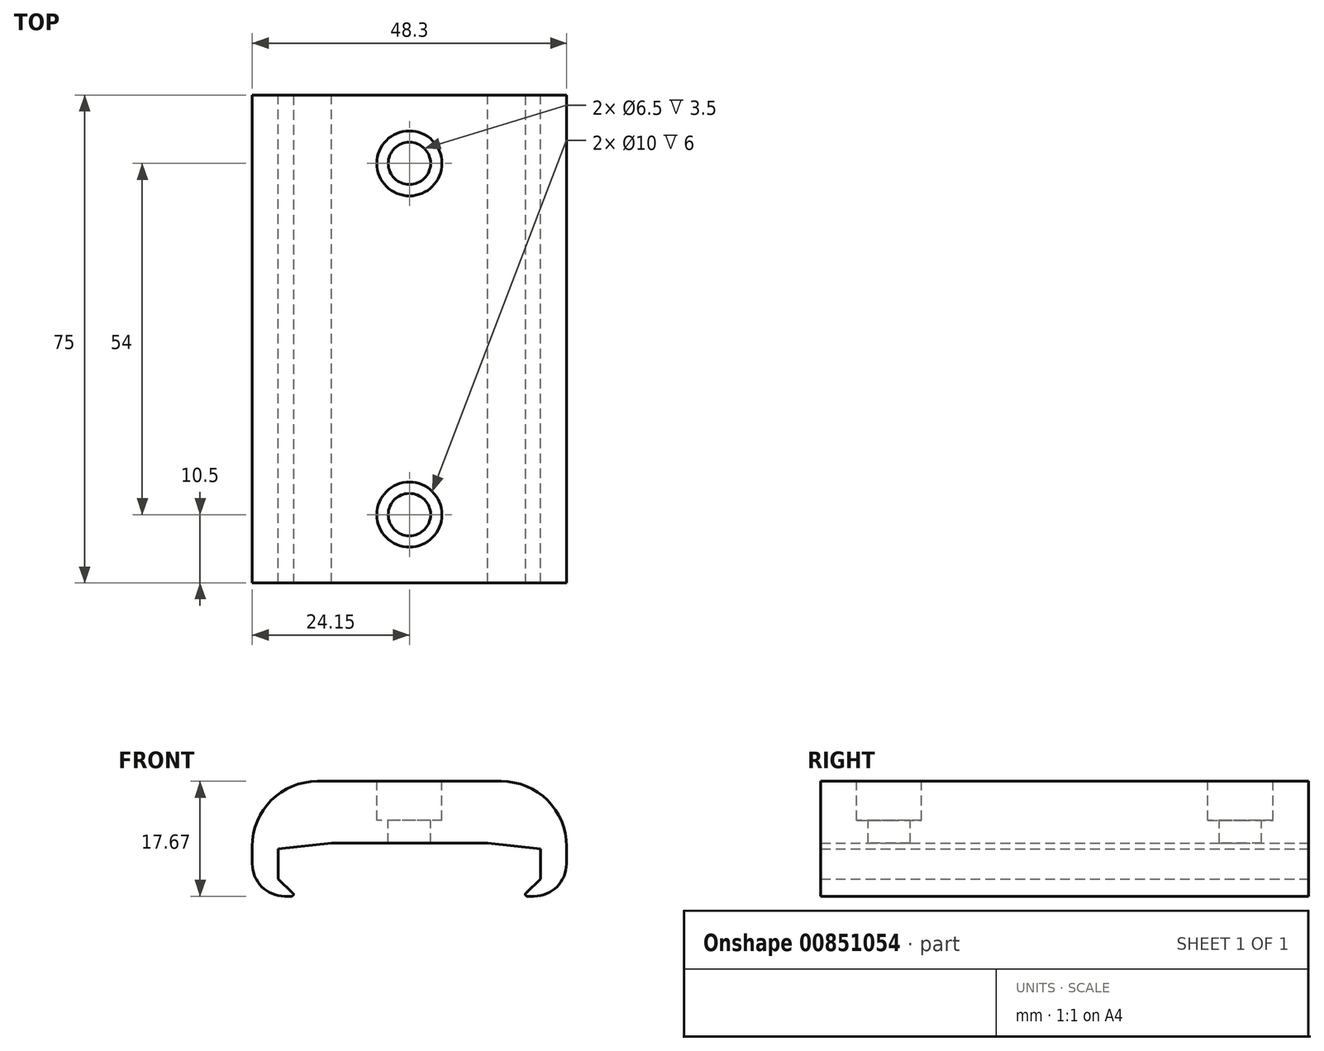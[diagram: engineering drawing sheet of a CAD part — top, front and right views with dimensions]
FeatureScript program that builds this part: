
annotation { "Feature Type Name" : "Feature", "Feature Type Description" : "" }
export const myFeature = defineFeature(function(context is Context, id is Id, definition is map)
    precondition{}
    {
        {
            var Q0;
            Q0=qCreatedBy(makeId("Front.planeOp"),FACE);
            var sketch = newSketch(context, id + "F0", { "sketchPlane" : qUnion([Q0])});
            skLineSegment(sketch, "E0.bottom", {"start": v(-12, 5.5) * mm, "end": v(12, 5.5) * mm});
            skLineSegment(sketch, "E0.left", {"start": v(-20.15, 4.6) * mm, "end": v(-20.15, 0) * mm});
            skLineSegment(sketch, "E0.right", {"start": v(20.15, 4.6) * mm, "end": v(20.15, 0) * mm});
            skLineSegment(sketch, "E1.top", {"start": v(-24.15, 15) * mm, "end": v(24.15, 15) * mm});
            skLineSegment(sketch, "E1.left", {"start": v(-24.15, 0) * mm, "end": v(-24.15, 15) * mm});
            skLineSegment(sketch, "E1.right", {"start": v(24.15, 0) * mm, "end": v(24.15, 15) * mm});
            skLineSegment(sketch, "E2", {"start": v(0, 5.5) * mm, "end": v(12, 5.5) * mm, "construction": true});
            skLineSegment(sketch, "E3", {"start": v(12, 5.5) * mm, "end": v(-12, 5.5) * mm, "construction": true});
            skLineSegment(sketch, "E4", {"start": v(-20.15, 0) * mm, "end": v(-17.38, -2.67) * mm, "construction": true});
            skLineSegment(sketch, "E5", {"start": v(-17.38, -2.67) * mm, "end": v(-24.15, -2.67) * mm, "construction": true});
            skLineSegment(sketch, "E6", {"start": v(-24.15, -2.67) * mm, "end": v(-24.15, 0) * mm, "construction": true});
            skLineSegment(sketch, "E7", {"start": v(-24.15, 0) * mm, "end": v(-24.15, -2.67) * mm});
            skLineSegment(sketch, "E8", {"start": v(-17.38, -2.67) * mm, "end": v(-20.15, 0) * mm});
            skLineSegment(sketch, "E9", {"start": v(-17.38, -2.67) * mm, "end": v(-24.15, -2.67) * mm});
            skLineSegment(sketch, "E10.MirrorCS", {"start": v(17.38, -2.67) * mm, "end": v(24.15, -2.67) * mm});
            skLineSegment(sketch, "E11.MirrorCS", {"start": v(17.38, -2.67) * mm, "end": v(20.15, 0) * mm});
            skLineSegment(sketch, "E12.MirrorCS", {"start": v(24.15, 0) * mm, "end": v(24.15, -2.67) * mm});
            skLineSegment(sketch, "E13.MirrorCS", {"start": v(20.15, 0) * mm, "end": v(17.38, -2.67) * mm, "construction": true});
            skLineSegment(sketch, "E14.MirrorCS", {"start": v(17.38, -2.67) * mm, "end": v(24.15, -2.67) * mm, "construction": true});
            skLineSegment(sketch, "E15.MirrorCS", {"start": v(24.15, -2.67) * mm, "end": v(24.15, 0) * mm, "construction": true});
            skLineSegment(sketch, "E16", {"start": v(-12, 5.5) * mm, "end": v(-20.15, 4.6) * mm});
            skLineSegment(sketch, "E17.MirrorCS", {"start": v(12, 5.5) * mm, "end": v(20.15, 4.6) * mm});
            skPoint(sketch, "E18.orphan", {"position": v(-20.15, 5.5) * mm});
            skPoint(sketch, "E19.orphan", {"position": v(20.15, 5.5) * mm});
            skPoint(sketch, "E20.end.orphan", {"position": v(24.15, 0) * mm});
            skSolve(sketch);
        }
        {
            var Q0;
            Q0=makeQuery(id+"F0.imprint","IMPRINT",FACE,{"disambiguationData":[TD([[makeQuery(id+"F0.imprint","IMPRINT",EDGE,{"derivedFrom":sQuery(id+"F0.wireOp",EDGE,"E0.bottom")}),1.0]])]});
            extrude(context, id + "F1", {"entities" : qUnion([Q0]), "depth" : 75 * mm, "offsetDistance" : 25 * mm});
        }
        {
            var Q0;
            Q0=makeQuery(id+"F1.opExtrude","SWEPT_EDGE",EDGE,{"disambiguationData":[OSD([sQuery(id+"F0.wireOp",EDGE,"E8"),sQuery(id+"F0.wireOp",EDGE,"E9")])]});
            var Q1;
            Q1=makeQuery(id+"F1.opExtrude","SWEPT_EDGE",EDGE,{"disambiguationData":[OSD([sQuery(id+"F0.wireOp",EDGE,"E10.MirrorCS"),sQuery(id+"F0.wireOp",EDGE,"E11.MirrorCS")])]});
            fillet(context, id + "F2", {"entities" : qUnion([Q0, Q1]), "tangentPropagation" : true, "radius" : 0.3 * mm, "defaultsChanged" : true, "vertexSettings" : [], "allowEdgeOverflow" : false});
        }
        {
            var Q0;
            Q0=makeQuery(id+"F1.opExtrude","SWEPT_EDGE",EDGE,{"disambiguationData":[OSD([sQuery(id+"F0.wireOp",EDGE,"E1.top"),sQuery(id+"F0.wireOp",EDGE,"E1.left")])]});
            var Q1;
            Q1=makeQuery(id+"F1.opExtrude","SWEPT_EDGE",EDGE,{"disambiguationData":[OSD([sQuery(id+"F0.wireOp",EDGE,"E1.top"),sQuery(id+"F0.wireOp",EDGE,"E1.right")])]});
            fillet(context, id + "F3", {"entities" : qUnion([Q0, Q1]), "tangentPropagation" : true, "radius" : 10 * mm, "defaultsChanged" : true, "vertexSettings" : [], "allowEdgeOverflow" : false});
        }
        {
            var Q0;
            Q0=makeQuery(id+"F1.opExtrude","SWEPT_EDGE",EDGE,{"disambiguationData":[OSD([sQuery(id+"F0.wireOp",EDGE,"E7"),sQuery(id+"F0.wireOp",EDGE,"E9")])]});
            var Q1;
            Q1=makeQuery(id+"F1.opExtrude","SWEPT_EDGE",EDGE,{"disambiguationData":[OSD([sQuery(id+"F0.wireOp",EDGE,"E10.MirrorCS"),sQuery(id+"F0.wireOp",EDGE,"E12.MirrorCS")])]});
            fillet(context, id + "F4", {"entities" : qUnion([Q0, Q1]), "tangentPropagation" : true, "radius" : 5 * mm, "defaultsChanged" : false, "vertexSettings" : [], "allowEdgeOverflow" : false});
        }
        {
            var Q0;
            Q0=makeQuery(id+"F1.opExtrude","SWEPT_BODY",BODY,{"disambiguationData":[OSD([sQuery(id+"F0.wireOp",EDGE,"E0.bottom"),sQuery(id+"F0.wireOp",EDGE,"E0.left"),sQuery(id+"F0.wireOp",EDGE,"E0.right"),sQuery(id+"F0.wireOp",EDGE,"E1.top"),sQuery(id+"F0.wireOp",EDGE,"E1.left"),sQuery(id+"F0.wireOp",EDGE,"E1.right"),sQuery(id+"F0.wireOp",EDGE,"E7"),sQuery(id+"F0.wireOp",EDGE,"E8"),sQuery(id+"F0.wireOp",EDGE,"E9"),sQuery(id+"F0.wireOp",EDGE,"E10.MirrorCS"),sQuery(id+"F0.wireOp",EDGE,"E11.MirrorCS"),sQuery(id+"F0.wireOp",EDGE,"E12.MirrorCS"),sQuery(id+"F0.wireOp",EDGE,"E16"),sQuery(id+"F0.wireOp",EDGE,"E17.MirrorCS")])]});
            transform(context, id + "F5", {"entities" : qUnion([Q0]), "transformType" : TransformType.TRANSLATION_3D, "dx" : 0 * mm, "dy" : 37.5 * mm, "dz" : 0 * mm, "makeCopy" : false});
        }
        {
            var Q0;
            Q0=makeQuery(id+"F1.opExtrude","SWEPT_FACE",FACE,{"disambiguationData":[OSD([sQuery(id+"F0.wireOp",EDGE,"E1.top")])]});
            var sketch = newSketch(context, id + "F6", { "sketchPlane" : qUnion([Q0])});
            skLineSegment(sketch, "E21", {"start": v(0, 0) * mm, "end": v(0, -27) * mm, "construction": true});
            skLineSegment(sketch, "E22", {"start": v(0, -27) * mm, "end": v(0, 0) * mm, "construction": true});
            skLineSegment(sketch, "E23", {"start": v(0, 0) * mm, "end": v(0, 27) * mm, "construction": true});
            skCircle(sketch, "E24", {"center": v(0, 27) * mm, "radius": 3.25 * mm});
            skCircle(sketch, "E25", {"center": v(0, -27) * mm, "radius": 3.25 * mm});
            skSolve(sketch);
        }
        {
            var Q0;
            Q0=makeQuery(id+"F6.imprint","IMPRINT",FACE,{"disambiguationData":[TD([[makeQuery(id+"F6.imprint","IMPRINT",EDGE,{"derivedFrom":sQuery(id+"F6.wireOp",EDGE,"E24")}),1.0]])]});
            var Q1;
            Q1=makeQuery(id+"F6.imprint","IMPRINT",FACE,{"disambiguationData":[TD([[makeQuery(id+"F6.imprint","IMPRINT",EDGE,{"derivedFrom":sQuery(id+"F6.wireOp",EDGE,"E25")}),1.0]])]});
            extrude(context, id + "F7", {"entities" : qUnion([Q0, Q1]), "operationType" : NewBodyOperationType.REMOVE, "oppositeDirection" : true, "depth" : 25 * mm, "offsetDistance" : 25 * mm});
        }
        {
            var Q0;
            Q0=makeQuery(id+"F1.opExtrude","SWEPT_FACE",FACE,{"disambiguationData":[OSD([sQuery(id+"F0.wireOp",EDGE,"E1.top")])]});
            var sketch = newSketch(context, id + "F8", { "sketchPlane" : qUnion([Q0])});
            skCircle(sketch, "E26", {"center": v(0, 27) * mm, "radius": 5 * mm});
            skCircle(sketch, "E27", {"center": v(0, -27) * mm, "radius": 5 * mm});
            skSolve(sketch);
        }
        {
            var Q0;
            Q0=makeQuery(id+"F8.imprint","IMPRINT",FACE,{"disambiguationData":[TD([[makeQuery(id+"F8.imprint","IMPRINT",EDGE,{"derivedFrom":sQuery(id+"F8.wireOp",EDGE,"E26")}),1.0]])]});
            var Q1;
            Q1=makeQuery(id+"F8.imprint","IMPRINT",FACE,{"disambiguationData":[TD([[makeQuery(id+"F8.imprint","IMPRINT",EDGE,{"derivedFrom":sQuery(id+"F8.wireOp",EDGE,"E27")}),1.0]])]});
            extrude(context, id + "F9", {"entities" : qUnion([Q0, Q1]), "operationType" : NewBodyOperationType.REMOVE, "oppositeDirection" : true, "depth" : 6 * mm, "offsetDistance" : 25 * mm});
        }
        {
            var Q0;
            Q0=makeQuery(id+"F1.opExtrude","SWEPT_BODY",BODY,{"disambiguationData":[OSD([sQuery(id+"F0.wireOp",EDGE,"E0.bottom"),sQuery(id+"F0.wireOp",EDGE,"E0.left"),sQuery(id+"F0.wireOp",EDGE,"E0.right"),sQuery(id+"F0.wireOp",EDGE,"E1.top"),sQuery(id+"F0.wireOp",EDGE,"E1.left"),sQuery(id+"F0.wireOp",EDGE,"E1.right"),sQuery(id+"F0.wireOp",EDGE,"E7"),sQuery(id+"F0.wireOp",EDGE,"E8"),sQuery(id+"F0.wireOp",EDGE,"E9"),sQuery(id+"F0.wireOp",EDGE,"E10.MirrorCS"),sQuery(id+"F0.wireOp",EDGE,"E11.MirrorCS"),sQuery(id+"F0.wireOp",EDGE,"E12.MirrorCS"),sQuery(id+"F0.wireOp",EDGE,"E16"),sQuery(id+"F0.wireOp",EDGE,"E17.MirrorCS")])]});
            transform(context, id + "F10", {"entities" : qUnion([Q0]), "transformType" : TransformType.TRANSLATION_3D, "dx" : 0 * mm, "dy" : 0 * mm, "dz" : -15 * mm, "makeCopy" : false});
        }
    });
